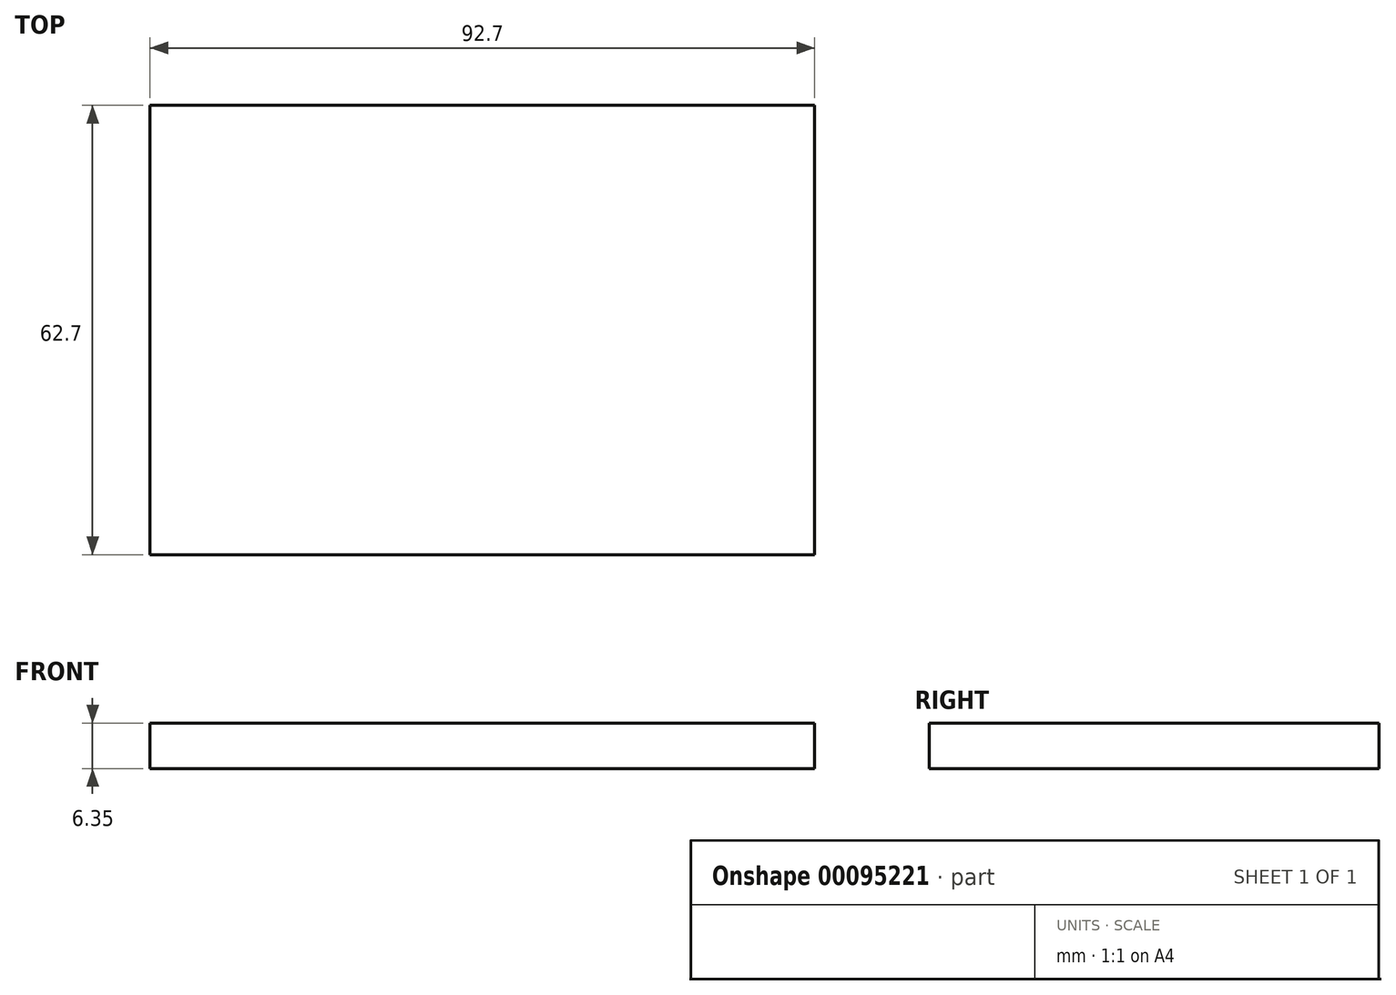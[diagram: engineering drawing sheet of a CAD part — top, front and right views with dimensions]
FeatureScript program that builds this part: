
annotation { "Feature Type Name" : "Feature", "Feature Type Description" : "" }
export const myFeature = defineFeature(function(context is Context, id is Id, definition is map)
    precondition{}
    {
        {
            var Q0;
            Q0=qCreatedBy(makeId("Top.planeOp"),FACE);
            var sketch = newSketch(context, id + "F0", { "sketchPlane" : qUnion([Q0])});
            skLineSegment(sketch, "E0.bottom", {"start": v(46.35, 31.35) * mm, "end": v(-46.35, 31.35) * mm});
            skLineSegment(sketch, "E0.top", {"start": v(46.35, -31.35) * mm, "end": v(-46.35, -31.35) * mm});
            skLineSegment(sketch, "E0.left", {"start": v(46.35, 31.35) * mm, "end": v(46.35, -31.35) * mm});
            skLineSegment(sketch, "E0.right", {"start": v(-46.35, 31.35) * mm, "end": v(-46.35, -31.35) * mm});
            skPoint(sketch, "E0.middle", {"position": v(0, 0) * mm});
            skPoint(sketch, "E1.bottom.end.orphan", {"position": v(-20, 20) * mm});
            skPoint(sketch, "E1.left.start.orphan", {"position": v(20, 20) * mm});
            skPoint(sketch, "E1.top.end.orphan", {"position": v(-20, -20) * mm});
            skPoint(sketch, "E1.top.start.orphan", {"position": v(20, -20) * mm});
            skSolve(sketch);
        }
        {
            var Q0;
            Q0=makeQuery(id+"F0.imprint","IMPRINT",FACE,{"disambiguationData":[TD([[makeQuery(id+"F0.imprint","IMPRINT",EDGE,{"derivedFrom":sQuery(id+"F0.wireOp",EDGE,"E0.bottom")}),1.0]])]});
            extrude(context, id + "F1", {"entities" : qUnion([Q0]), "depth" : 6.35 * mm});
        }
    });
